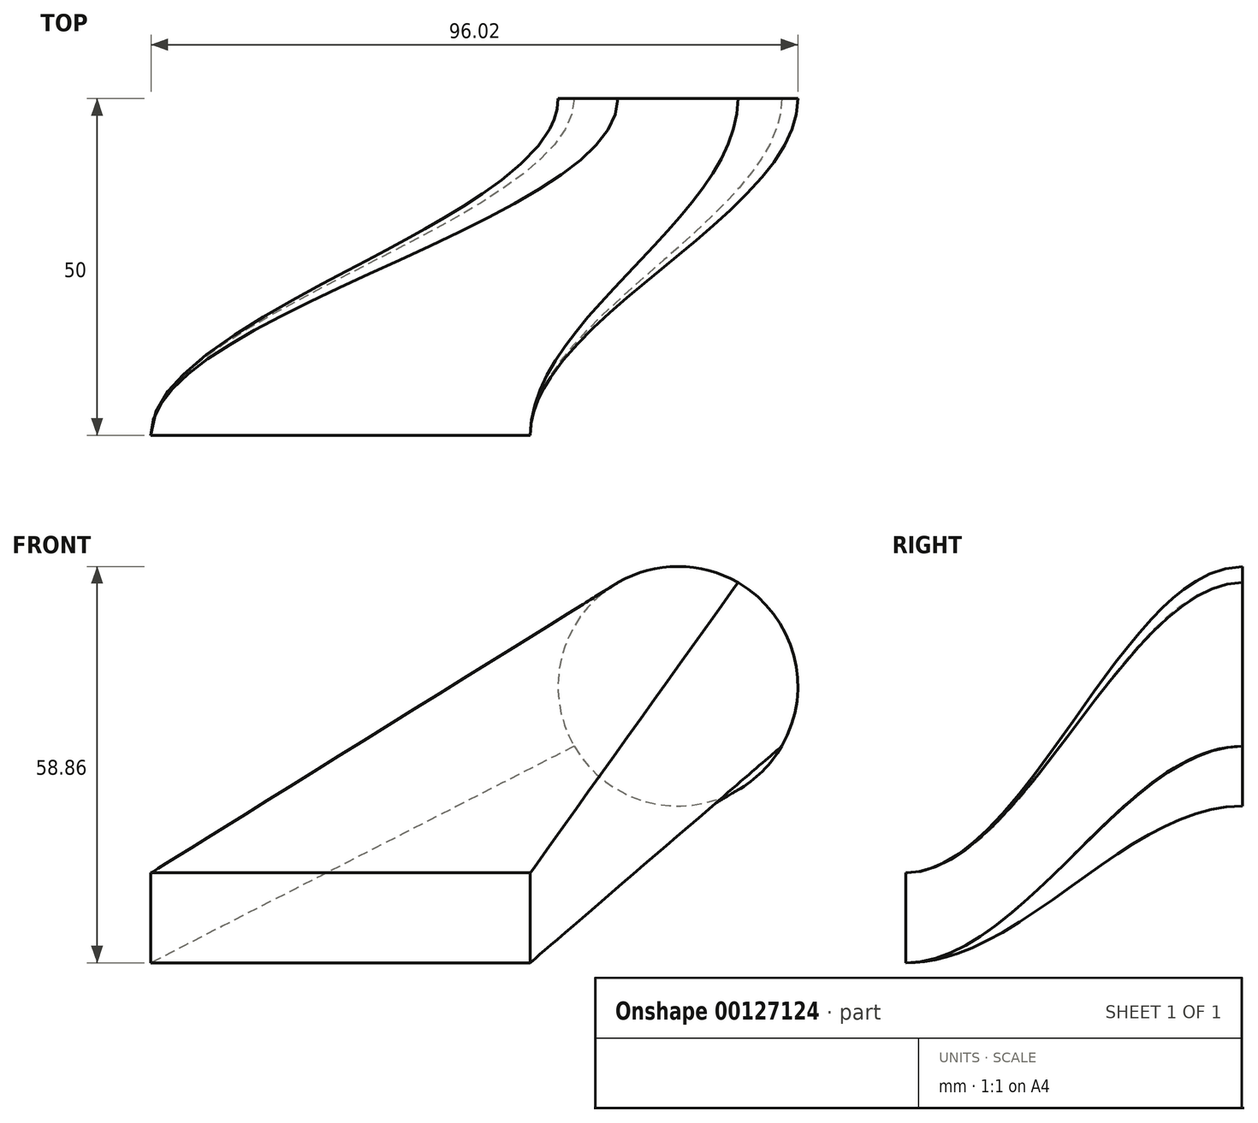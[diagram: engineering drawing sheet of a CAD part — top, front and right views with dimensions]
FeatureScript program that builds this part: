
annotation { "Feature Type Name" : "Feature", "Feature Type Description" : "" }
export const myFeature = defineFeature(function(context is Context, id is Id, definition is map)
    precondition{}
    {
        {
            var Q0;
            Q0=qCreatedBy(makeId("Front.planeOp"),FACE);
            var sketch = newSketch(context, id + "F0", { "sketchPlane" : qUnion([Q0])});
            skArc(sketch, "E0", {"start": v(-25.58, 35.31) * mm, "mid": v(-34.47, 37.7) * mm, "end": v(-43.37, 35.31) * mm});
            skArc(sketch, "E1", {"start": v(-43.37, 35.31) * mm, "mid": v(-51.66, 24.51) * mm, "end": v(-49.88, 11) * mm});
            skArc(sketch, "E2", {"start": v(-49.88, 11) * mm, "mid": v(-34.47, 2.11) * mm, "end": v(-19.06, 11) * mm});
            skArc(sketch, "E3", {"start": v(-19.06, 11) * mm, "mid": v(-17.28, 24.51) * mm, "end": v(-25.58, 35.31) * mm});
            skLineSegment(sketch, "E4", {"start": v(-34.47, 19.9) * mm, "end": v(-34.47, 65.05) * mm, "construction": true});
            skLineSegment(sketch, "E5", {"start": v(-34.47, 19.9) * mm, "end": v(-43.37, 35.31) * mm, "construction": true});
            skLineSegment(sketch, "E6", {"start": v(-34.47, 19.9) * mm, "end": v(-49.88, 11) * mm, "construction": true});
            skLineSegment(sketch, "E7", {"start": v(-34.47, 19.9) * mm, "end": v(-25.58, 35.31) * mm, "construction": true});
            skLineSegment(sketch, "E8", {"start": v(-34.47, 19.9) * mm, "end": v(-19.06, 11) * mm, "construction": true});
            skSolve(sketch);
        }
        {
            var Q0;
            Q0=makeQuery(id+"F0.imprint","IMPRINT",FACE,{"disambiguationData":[TD([[makeQuery(id+"F0.imprint","IMPRINT",EDGE,{"derivedFrom":sQuery(id+"F0.wireOp",EDGE,"E0")}),1.0]])]});
            cPlane(context, id + "F1", {"entities" : qUnion([Q0]), "cplaneType" : CPlaneType.OFFSET, "offset" : 50 * mm, "width" : 150 * mm, "height" : 150 * mm});
        }
        {
            var Q0;
            Q0=qCreatedBy(id+"F1.planeOp",FACE);
            var sketch = newSketch(context, id + "F2", { "sketchPlane" : qUnion([Q0])});
            skLineSegment(sketch, "E9.bottom", {"start": v(-112.7, -7.8) * mm, "end": v(-56.4, -7.8) * mm});
            skLineSegment(sketch, "E9.top", {"start": v(-112.7, -21.16) * mm, "end": v(-56.4, -21.16) * mm});
            skLineSegment(sketch, "E9.left", {"start": v(-112.7, -7.8) * mm, "end": v(-112.7, -21.16) * mm});
            skLineSegment(sketch, "E9.right", {"start": v(-56.4, -7.8) * mm, "end": v(-56.4, -21.16) * mm});
            skSolve(sketch);
        }
        {
            var Q0;
            Q0=makeQuery(id+"F0.imprint","IMPRINT",FACE,{"disambiguationData":[TD([[makeQuery(id+"F0.imprint","IMPRINT",EDGE,{"derivedFrom":sQuery(id+"F0.wireOp",EDGE,"E0")}),1.0]])]});
            var Q1;
            Q1=makeQuery(id+"F2.imprint","IMPRINT",FACE,{"disambiguationData":[TD([[makeQuery(id+"F2.imprint","IMPRINT",EDGE,{"derivedFrom":sQuery(id+"F2.wireOp",EDGE,"E9.bottom")}),-1.0]])]});
            loft(context, id + "F3", {"startCondition" : LoftEndDerivativeType.NORMAL_TO_PROFILE, "startMagnitude" : 1, "endCondition" : LoftEndDerivativeType.NORMAL_TO_PROFILE, "endMagnitude" : 1, "sheetProfilesArray" : [{ "sheetProfileEntities" : qUnion([Q0]) }, { "sheetProfileEntities" : qUnion([Q1]) }]});
        }
    });
